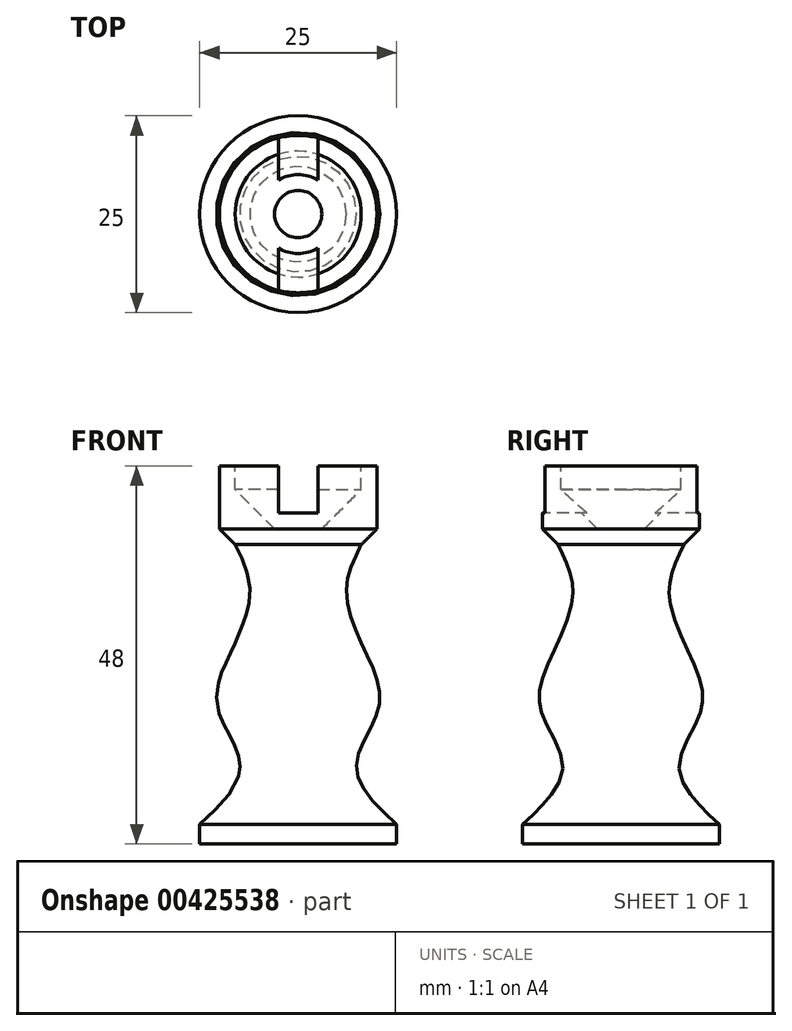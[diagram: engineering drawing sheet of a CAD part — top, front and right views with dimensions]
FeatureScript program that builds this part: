
annotation { "Feature Type Name" : "Feature", "Feature Type Description" : "" }
export const myFeature = defineFeature(function(context is Context, id is Id, definition is map)
    precondition{}
    {
        {
            var Q0;
            Q0=qCreatedBy(makeId("Front.planeOp"),FACE);
            var sketch = newSketch(context, id + "F0", { "sketchPlane" : qUnion([Q0])});
            skLineSegment(sketch, "E0.bottom", {"start": v(12.5, 48) * mm, "end": v(0, 48) * mm});
            skLineSegment(sketch, "E0.top", {"start": v(12.5, 0) * mm, "end": v(0, 0) * mm});
            skLineSegment(sketch, "E0.left", {"start": v(12.5, 48) * mm, "end": v(12.5, 0) * mm});
            skLineSegment(sketch, "E0.right", {"start": v(0, 48) * mm, "end": v(0, 0) * mm});
            skLineSegment(sketch, "E1.bottom", {"start": v(0, 48) * mm, "end": v(8, 48) * mm});
            skLineSegment(sketch, "E1.top", {"start": v(0, 40) * mm, "end": v(8, 40) * mm});
            skLineSegment(sketch, "E1.left", {"start": v(0, 48) * mm, "end": v(0, 40) * mm});
            skLineSegment(sketch, "E1.right", {"start": v(8, 48) * mm, "end": v(8, 40) * mm});
            skLineSegment(sketch, "E2", {"start": v(10, 48) * mm, "end": v(10, 38) * mm});
            skLineSegment(sketch, "E3", {"start": v(10, 38) * mm, "end": v(0, 38) * mm});
            skLineSegment(sketch, "E4", {"start": v(10, 40) * mm, "end": v(8, 38) * mm});
            skLineSegment(sketch, "E5", {"start": v(0, 2.5) * mm, "end": v(12.5, 2.5) * mm});
            skFitSpline(sketch, "E6", {"points": [v(8, 38) * mm, v(6.1, 31.93) * mm, v(8.79, 23.89) * mm, v(10.24, 17.27) * mm, v(7.38, 9.92) * mm, v(12.5, 2.5) * mm], "startDerivative": vector(-15.52, -32.45) * mm, "endDerivative": vector(38.77, -35.16) * mm});
            skSolve(sketch);
        }
        {
            var Q0;
            {var subQ3=sQuery(id+"F0.wireOp",EDGE,"E5");Q0=makeQuery(id+"F0.imprint","IMPRINT",FACE,{"disambiguationData":[TD([[makeQuery(id+"F0.imprint","IMPRINT",EDGE,{"derivedFrom":subQ3}),1.0]])]});}
            var Q1;
            {var subQ0=sQuery(id+"F0.wireOp",EDGE,"E0.top");Q1=makeQuery(id+"F0.imprint","IMPRINT",FACE,{"disambiguationData":[TD([[makeQuery(id+"F0.imprint","IMPRINT",EDGE,{"derivedFrom":subQ0}),-1.0]])]});}
            var Q2;
            {var subQ0=sQuery(id+"F0.wireOp",EDGE,"E1.top");Q2=makeQuery(id+"F0.imprint","IMPRINT",FACE,{"disambiguationData":[TD([[makeQuery(id+"F0.imprint","IMPRINT",EDGE,{"derivedFrom":subQ0}),-1.0]])]});}
            var Q3;
            Q3=sQuery(id+"F0.wireOp",EDGE,"E1.left");
            revolve(context, id + "F1", {"entities" : qUnion([Q0, Q1, Q2]), "axis" : qUnion([Q3]), "revolveType" : RevolveType.FULL});
        }
        {
            var Q0;
            Q0=makeQuery(id+"F1.opRevolve","SWEPT_FACE",FACE,{"disambiguationData":[OSD([sQuery(id+"F0.wireOp",EDGE,"E0.bottom")])]});
            var sketch = newSketch(context, id + "F2", { "sketchPlane" : qUnion([Q0])});
            skLineSegment(sketch, "E7.bottom", {"start": v(-2.5, 15) * mm, "end": v(2.5, 15) * mm});
            skLineSegment(sketch, "E7.top", {"start": v(-2.5, -15) * mm, "end": v(2.5, -15) * mm});
            skLineSegment(sketch, "E7.left", {"start": v(-2.5, 15) * mm, "end": v(-2.5, -15) * mm});
            skLineSegment(sketch, "E7.right", {"start": v(2.5, 15) * mm, "end": v(2.5, -15) * mm});
            skPoint(sketch, "E7.middle", {"position": v(0, 0) * mm});
            skSolve(sketch);
        }
        {
            var Q0;
            Q0 = qSketchRegion(id + "F2", true);
            extrude(context, id + "F3", {"entities" : qUnion([Q0]), "operationType" : NewBodyOperationType.REMOVE, "oppositeDirection" : true, "depth" : 6 * mm});
        }
        {
            var Q0;
            Q0=makeQuery(id+"F1.opRevolve","SWEPT_FACE",FACE,{"disambiguationData":[OSD([sQuery(id+"F0.wireOp",EDGE,"E1.top")])]});
            chamfer(context, id + "F4", {"entities" : qUnion([Q0]), "width" : 5 * mm, "tangentPropagation" : true});
        }
    });
